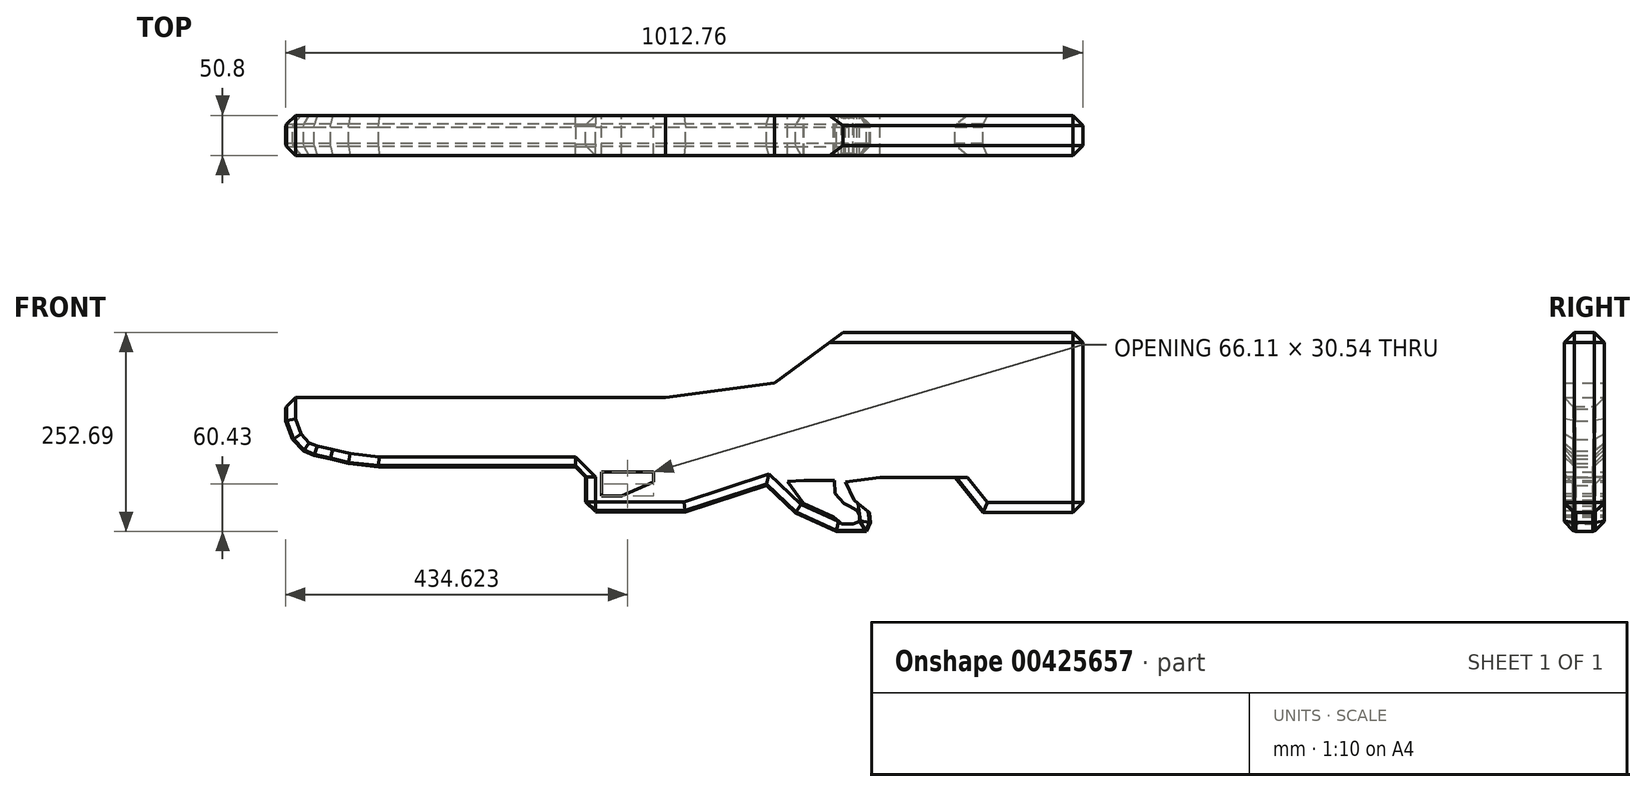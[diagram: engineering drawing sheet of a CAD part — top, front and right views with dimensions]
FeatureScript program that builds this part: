
annotation { "Feature Type Name" : "Feature", "Feature Type Description" : "" }
export const myFeature = defineFeature(function(context is Context, id is Id, definition is map)
    precondition{}
    {
        {
            var Q0;
            Q0=qCreatedBy(makeId("Front.planeOp"),FACE);
            var sketch = newSketch(context, id + "F0", { "sketchPlane" : qUnion([Q0])});
            skLineSegment(sketch, "E0", {"start": v(-56.13, -82.02) * mm, "end": v(-158.8, -115.37) * mm});
            skLineSegment(sketch, "E1", {"start": v(-158.8, -115.37) * mm, "end": v(-285.8, -115.37) * mm});
            skLineSegment(sketch, "E2", {"start": v(-285.8, -115.37) * mm, "end": v(-285.8, -58.22) * mm});
            skLineSegment(sketch, "E3", {"start": v(-285.8, -58.22) * mm, "end": v(-514.4, -58.22) * mm});
            skLineSegment(sketch, "E4", {"start": v(-666.8, 29.79) * mm, "end": v(-285.8, 29.79) * mm});
            skLineSegment(sketch, "E5", {"start": v(218.96, -116.33) * mm, "end": v(345.96, -116.33) * mm});
            skLineSegment(sketch, "E6", {"start": v(345.96, -116.33) * mm, "end": v(345.96, 112.27) * mm});
            skLineSegment(sketch, "E7", {"start": v(345.96, 112.27) * mm, "end": v(41.16, 112.27) * mm});
            skLineSegment(sketch, "E8", {"start": v(41.16, 112.27) * mm, "end": v(-45.72, 48.19) * mm});
            skLineSegment(sketch, "E9", {"start": v(-45.72, 48.19) * mm, "end": v(-184.2, 29.79) * mm});
            skLineSegment(sketch, "E10", {"start": v(-184.2, 29.79) * mm, "end": v(-285.8, 29.79) * mm});
            skLineSegment(sketch, "E11", {"start": v(-265.23, -64.72) * mm, "end": v(-265.23, -95.26) * mm});
            skLineSegment(sketch, "E12", {"start": v(-265.23, -95.26) * mm, "end": v(-239.83, -95.26) * mm});
            skLineSegment(sketch, "E13", {"start": v(-239.83, -95.26) * mm, "end": v(-199.12, -77.42) * mm});
            skLineSegment(sketch, "E14", {"start": v(-199.12, -77.42) * mm, "end": v(-199.12, -64.72) * mm});
            skLineSegment(sketch, "E15", {"start": v(-199.12, -64.72) * mm, "end": v(-265.23, -64.72) * mm});
            skLineSegment(sketch, "E16", {"start": v(-56.13, -82.02) * mm, "end": v(-19.03, -116.73) * mm});
            skLineSegment(sketch, "E17", {"start": v(-19.03, -116.73) * mm, "end": v(32.98, -140.42) * mm});
            skLineSegment(sketch, "E18", {"start": v(32.98, -140.42) * mm, "end": v(71.08, -140.42) * mm});
            skLineSegment(sketch, "E19", {"start": v(218.96, -116.33) * mm, "end": v(183.53, -71.5) * mm});
            skLineSegment(sketch, "E20", {"start": v(183.53, -71.5) * mm, "end": v(88.28, -71.5) * mm});
            skLineSegment(sketch, "E21", {"start": v(88.28, -71.5) * mm, "end": v(44.21, -77.35) * mm});
            skLineSegment(sketch, "E22", {"start": v(44.21, -77.35) * mm, "end": v(55.1, -100.3) * mm});
            skLineSegment(sketch, "E23", {"start": v(55.1, -100.3) * mm, "end": v(74.8, -116.33) * mm});
            skLineSegment(sketch, "E24", {"start": v(74.8, -116.33) * mm, "end": v(76.46, -128.92) * mm});
            skLineSegment(sketch, "E25", {"start": v(76.46, -128.92) * mm, "end": v(71.08, -140.42) * mm});
            skLineSegment(sketch, "E26", {"start": v(-29.05, -77.07) * mm, "end": v(-8.71, -104.67) * mm});
            skLineSegment(sketch, "E27", {"start": v(-8.71, -104.67) * mm, "end": v(29.47, -122.07) * mm});
            skLineSegment(sketch, "E28", {"start": v(42.4, -104.75) * mm, "end": v(31, -91.88) * mm});
            skLineSegment(sketch, "E29", {"start": v(31, -91.88) * mm, "end": v(30.46, -75.77) * mm});
            skLineSegment(sketch, "E30", {"start": v(30.46, -75.77) * mm, "end": v(-8.19, -75.77) * mm});
            skLineSegment(sketch, "E31", {"start": v(-8.19, -75.77) * mm, "end": v(-29.05, -77.07) * mm});
            skLineSegment(sketch, "E32", {"start": v(29.47, -122.07) * mm, "end": v(39.46, -130.68) * mm});
            skLineSegment(sketch, "E33", {"start": v(39.46, -130.68) * mm, "end": v(54.19, -130.68) * mm});
            skLineSegment(sketch, "E34", {"start": v(54.19, -130.68) * mm, "end": v(62.35, -127.97) * mm});
            skLineSegment(sketch, "E35", {"start": v(62.35, -127.97) * mm, "end": v(62.35, -122.07) * mm});
            skLineSegment(sketch, "E36", {"start": v(62.35, -122.07) * mm, "end": v(62.35, -119.65) * mm});
            skLineSegment(sketch, "E37", {"start": v(62.35, -119.65) * mm, "end": v(59.02, -113.61) * mm});
            skLineSegment(sketch, "E38", {"start": v(59.02, -113.61) * mm, "end": v(49.26, -108.1) * mm});
            skLineSegment(sketch, "E39", {"start": v(49.26, -108.1) * mm, "end": v(42.4, -104.75) * mm});
            skLineSegment(sketch, "E40", {"start": v(-666.8, 29.79) * mm, "end": v(-666.8, 0) * mm});
            skLineSegment(sketch, "E41", {"start": v(-666.8, 0) * mm, "end": v(-658, -23.58) * mm});
            skLineSegment(sketch, "E42", {"start": v(-658, -23.58) * mm, "end": v(-643.96, -38.44) * mm});
            skLineSegment(sketch, "E43", {"start": v(-514.4, -58.22) * mm, "end": v(-548.47, -58.22) * mm});
            skLineSegment(sketch, "E44", {"start": v(-548.47, -58.22) * mm, "end": v(-586.77, -53.93) * mm});
            skLineSegment(sketch, "E45", {"start": v(-586.77, -53.93) * mm, "end": v(-609.74, -48.34) * mm});
            skLineSegment(sketch, "E46", {"start": v(-609.74, -48.34) * mm, "end": v(-630.48, -44.18) * mm});
            skLineSegment(sketch, "E47", {"start": v(-630.48, -44.18) * mm, "end": v(-643.96, -38.44) * mm});
            skSolve(sketch);
        }
        {
            var Q0;
            Q0 = qSketchRegion(id + "F0", true);
            extrude(context, id + "F1", {"entities" : qUnion([Q0]), "depth" : 50.8 * mm});
        }
        {
            var Q0;
            Q0=makeQuery(id+"F1.opExtrude","CAP_EDGE",EDGE,{"disambiguationData":[OSD([sQuery(id+"F0.wireOp",EDGE,"E7")])],"isStart":true});
            var Q1;
            Q1=makeQuery(id+"F1.opExtrude","CAP_EDGE",EDGE,{"disambiguationData":[OSD([sQuery(id+"F0.wireOp",EDGE,"E7")])],"isStart":false});
            var Q2;
            Q2=makeQuery(id+"F1.opExtrude","CAP_EDGE",EDGE,{"disambiguationData":[OSD([sQuery(id+"F0.wireOp",EDGE,"E6")])],"isStart":false});
            var Q3;
            Q3=makeQuery(id+"F1.opExtrude","CAP_EDGE",EDGE,{"disambiguationData":[OSD([sQuery(id+"F0.wireOp",EDGE,"E6")])],"isStart":true});
            var Q4;
            Q4=makeQuery(id+"F1.opExtrude","SWEPT_EDGE",EDGE,{"disambiguationData":[OSD([sQuery(id+"F0.wireOp",EDGE,"E6"),sQuery(id+"F0.wireOp",EDGE,"E7")])]});
            var Q5;
            Q5=makeQuery(id+"F1.opExtrude","SWEPT_EDGE",EDGE,{"disambiguationData":[OSD([sQuery(id+"F0.wireOp",EDGE,"E5"),sQuery(id+"F0.wireOp",EDGE,"E6")])]});
            var Q6;
            Q6=makeQuery(id+"F1.opExtrude","CAP_EDGE",EDGE,{"disambiguationData":[OSD([sQuery(id+"F0.wireOp",EDGE,"E5")])],"isStart":true});
            var Q7;
            Q7=makeQuery(id+"F1.opExtrude","CAP_EDGE",EDGE,{"disambiguationData":[OSD([sQuery(id+"F0.wireOp",EDGE,"E5")])],"isStart":false});
            var Q8;
            Q8=makeQuery(id+"F1.opExtrude","CAP_EDGE",EDGE,{"disambiguationData":[OSD([sQuery(id+"F0.wireOp",EDGE,"0iQW84Cc-BR3S-5Jue-mCoC-AWeY4tAWd9hm")])],"isStart":true});
            var Q9;
            Q9=makeQuery(id+"F1.opExtrude","CAP_EDGE",EDGE,{"disambiguationData":[OSD([sQuery(id+"F0.wireOp",EDGE,"0iQW84Cc-BR3S-5Jue-mCoC-AWeY4tAWd9hm")])],"isStart":false});
            var Q10;
            Q10=makeQuery(id+"F1.opExtrude","CAP_EDGE",EDGE,{"disambiguationData":[OSD([sQuery(id+"F0.wireOp",EDGE,"J2oNxDXB-GuEv-2erL-x4Tu-Tdrz2HGzG4U1")])],"isStart":true});
            var Q11;
            Q11=makeQuery(id+"F1.opExtrude","CAP_EDGE",EDGE,{"disambiguationData":[OSD([sQuery(id+"F0.wireOp",EDGE,"J2oNxDXB-GuEv-2erL-x4Tu-Tdrz2HGzG4U1")])],"isStart":false});
            var Q12;
            Q12=makeQuery(id+"F1.opExtrude","CAP_EDGE",EDGE,{"disambiguationData":[OSD([sQuery(id+"F0.wireOp",EDGE,"E0")])],"isStart":true});
            var Q13;
            Q13=makeQuery(id+"F1.opExtrude","CAP_EDGE",EDGE,{"disambiguationData":[OSD([sQuery(id+"F0.wireOp",EDGE,"E0")])],"isStart":false});
            var Q14;
            Q14=makeQuery(id+"F1.opExtrude","CAP_EDGE",EDGE,{"disambiguationData":[OSD([sQuery(id+"F0.wireOp",EDGE,"E1")])],"isStart":true});
            var Q15;
            Q15=makeQuery(id+"F1.opExtrude","SWEPT_EDGE",EDGE,{"disambiguationData":[OSD([sQuery(id+"F0.wireOp",EDGE,"E1"),sQuery(id+"F0.wireOp",EDGE,"E2")])]});
            var Q16;
            Q16=makeQuery(id+"F1.opExtrude","CAP_EDGE",EDGE,{"disambiguationData":[OSD([sQuery(id+"F0.wireOp",EDGE,"E1")])],"isStart":false});
            var Q17;
            Q17=makeQuery(id+"F1.opExtrude","CAP_EDGE",EDGE,{"disambiguationData":[OSD([sQuery(id+"F0.wireOp",EDGE,"E3")])],"isStart":false});
            var Q18;
            Q18=makeQuery(id+"F1.opExtrude","CAP_EDGE",EDGE,{"disambiguationData":[OSD([sQuery(id+"F0.wireOp",EDGE,"E3")])],"isStart":true});
            var Q19;
            Q19=makeQuery(id+"F1.opExtrude","CAP_EDGE",EDGE,{"disambiguationData":[OSD([sQuery(id+"F0.wireOp",EDGE,"U8XlatA5-svrj-UKUK-BNE7-sDehN0CjtlMt")])],"isStart":false});
            var Q20;
            Q20=makeQuery(id+"F1.opExtrude","CAP_EDGE",EDGE,{"disambiguationData":[OSD([sQuery(id+"F0.wireOp",EDGE,"U8XlatA5-svrj-UKUK-BNE7-sDehN0CjtlMt")])],"isStart":true});
            var Q21;
            Q21=makeQuery(id+"F1.opExtrude","CAP_EDGE",EDGE,{"disambiguationData":[OSD([sQuery(id+"F0.wireOp",EDGE,"E2")])],"isStart":false});
            var Q22;
            Q22=makeQuery(id+"F1.opExtrude","CAP_EDGE",EDGE,{"disambiguationData":[OSD([sQuery(id+"F0.wireOp",EDGE,"E2")])],"isStart":true});
            var Q23;
            Q23=makeQuery(id+"F1.opExtrude","CAP_EDGE",EDGE,{"disambiguationData":[OSD([sQuery(id+"F0.wireOp",EDGE,"E19")])],"isStart":true});
            var Q24;
            Q24=makeQuery(id+"F1.opExtrude","CAP_EDGE",EDGE,{"disambiguationData":[OSD([sQuery(id+"F0.wireOp",EDGE,"E19")])],"isStart":false});
            var Q25;
            Q25=makeQuery(id+"F1.opExtrude","CAP_EDGE",EDGE,{"disambiguationData":[OSD([sQuery(id+"F0.wireOp",EDGE,"E16")])],"isStart":true});
            var Q26;
            Q26=makeQuery(id+"F1.opExtrude","CAP_EDGE",EDGE,{"disambiguationData":[OSD([sQuery(id+"F0.wireOp",EDGE,"E16")])],"isStart":false});
            var Q27;
            Q27=makeQuery(id+"F1.opExtrude","CAP_EDGE",EDGE,{"disambiguationData":[OSD([sQuery(id+"F0.wireOp",EDGE,"E17")])],"isStart":false});
            var Q28;
            Q28=makeQuery(id+"F1.opExtrude","CAP_EDGE",EDGE,{"disambiguationData":[OSD([sQuery(id+"F0.wireOp",EDGE,"E17")])],"isStart":true});
            var Q29;
            Q29=makeQuery(id+"F1.opExtrude","CAP_EDGE",EDGE,{"disambiguationData":[OSD([sQuery(id+"F0.wireOp",EDGE,"E18")])],"isStart":true});
            var Q30;
            Q30=makeQuery(id+"F1.opExtrude","CAP_EDGE",EDGE,{"disambiguationData":[OSD([sQuery(id+"F0.wireOp",EDGE,"E18")])],"isStart":false});
            var Q31;
            Q31=makeQuery(id+"F1.opExtrude","CAP_EDGE",EDGE,{"disambiguationData":[OSD([sQuery(id+"F0.wireOp",EDGE,"E25")])],"isStart":true});
            var Q32;
            Q32=makeQuery(id+"F1.opExtrude","CAP_EDGE",EDGE,{"disambiguationData":[OSD([sQuery(id+"F0.wireOp",EDGE,"E24")])],"isStart":true});
            var Q33;
            Q33=makeQuery(id+"F1.opExtrude","CAP_EDGE",EDGE,{"disambiguationData":[OSD([sQuery(id+"F0.wireOp",EDGE,"E25")])],"isStart":false});
            var Q34;
            Q34=makeQuery(id+"F1.opExtrude","CAP_EDGE",EDGE,{"disambiguationData":[OSD([sQuery(id+"F0.wireOp",EDGE,"E24")])],"isStart":false});
            var Q35;
            Q35=makeQuery(id+"F1.opExtrude","SWEPT_EDGE",EDGE,{"disambiguationData":[OSD([sQuery(id+"F0.wireOp",EDGE,"U8XlatA5-svrj-UKUK-BNE7-sDehN0CjtlMt"),sQuery(id+"F0.wireOp",EDGE,"E4")])]});
            var Q36;
            Q36=makeQuery(id+"F1.opExtrude","SWEPT_EDGE",EDGE,{"disambiguationData":[OSD([sQuery(id+"F0.wireOp",EDGE,"E3"),sQuery(id+"F0.wireOp",EDGE,"U8XlatA5-svrj-UKUK-BNE7-sDehN0CjtlMt")])]});
            var Q37;
            Q37=makeQuery(id+"F1.opExtrude","CAP_EDGE",EDGE,{"disambiguationData":[OSD([sQuery(id+"F0.wireOp",EDGE,"E44")])],"isStart":false});
            var Q38;
            Q38=makeQuery(id+"F1.opExtrude","CAP_EDGE",EDGE,{"disambiguationData":[OSD([sQuery(id+"F0.wireOp",EDGE,"E45")])],"isStart":false});
            var Q39;
            Q39=makeQuery(id+"F1.opExtrude","CAP_EDGE",EDGE,{"disambiguationData":[OSD([sQuery(id+"F0.wireOp",EDGE,"E47")])],"isStart":false});
            var Q40;
            Q40=makeQuery(id+"F1.opExtrude","CAP_EDGE",EDGE,{"disambiguationData":[OSD([sQuery(id+"F0.wireOp",EDGE,"E46")])],"isStart":false});
            var Q41;
            Q41=makeQuery(id+"F1.opExtrude","CAP_EDGE",EDGE,{"disambiguationData":[OSD([sQuery(id+"F0.wireOp",EDGE,"E42")])],"isStart":false});
            var Q42;
            Q42=makeQuery(id+"F1.opExtrude","CAP_EDGE",EDGE,{"disambiguationData":[OSD([sQuery(id+"F0.wireOp",EDGE,"E41")])],"isStart":false});
            var Q43;
            Q43=makeQuery(id+"F1.opExtrude","CAP_EDGE",EDGE,{"disambiguationData":[OSD([sQuery(id+"F0.wireOp",EDGE,"E40")])],"isStart":false});
            var Q44;
            Q44=makeQuery(id+"F1.opExtrude","CAP_EDGE",EDGE,{"disambiguationData":[OSD([sQuery(id+"F0.wireOp",EDGE,"E44")])],"isStart":true});
            var Q45;
            Q45=makeQuery(id+"F1.opExtrude","CAP_EDGE",EDGE,{"disambiguationData":[OSD([sQuery(id+"F0.wireOp",EDGE,"E45")])],"isStart":true});
            var Q46;
            Q46=makeQuery(id+"F1.opExtrude","CAP_EDGE",EDGE,{"disambiguationData":[OSD([sQuery(id+"F0.wireOp",EDGE,"E46")])],"isStart":true});
            var Q47;
            Q47=makeQuery(id+"F1.opExtrude","CAP_EDGE",EDGE,{"disambiguationData":[OSD([sQuery(id+"F0.wireOp",EDGE,"E47")])],"isStart":true});
            var Q48;
            Q48=makeQuery(id+"F1.opExtrude","CAP_EDGE",EDGE,{"disambiguationData":[OSD([sQuery(id+"F0.wireOp",EDGE,"E42")])],"isStart":true});
            var Q49;
            Q49=makeQuery(id+"F1.opExtrude","CAP_EDGE",EDGE,{"disambiguationData":[OSD([sQuery(id+"F0.wireOp",EDGE,"E41")])],"isStart":true});
            var Q50;
            Q50=makeQuery(id+"F1.opExtrude","CAP_EDGE",EDGE,{"disambiguationData":[OSD([sQuery(id+"F0.wireOp",EDGE,"E40")])],"isStart":true});
            chamfer(context, id + "F2", {"entities" : qUnion([Q0, Q1, Q2, Q3, Q4, Q5, Q6, Q7, Q8, Q9, Q10, Q11, Q12, Q13, Q14, Q15, Q16, Q17, Q18, Q19, Q20, Q21, Q22, Q23, Q24, Q25, Q26, Q27, Q28, Q29, Q30, Q31, Q32, Q33, Q34, Q35, Q36, Q37, Q38, Q39, Q40, Q41, Q42, Q43, Q44, Q45, Q46, Q47, Q48, Q49, Q50]), "width" : 12.7 * mm, "tangentPropagation" : true});
        }
        {
            var Q0;
            {var subQ0=sQuery(id+"F0.wireOp",EDGE,"E41");Q0=makeQuery(id+"F2.opChamfer","BLEND_EDGE",EDGE,{"blendedFrom":[makeQuery(id+"F1.opExtrude","CAP_EDGE",EDGE,{"disambiguationData":[OSD([subQ0])],"isStart":true}),makeQuery(id+"F1.opExtrude","SWEPT_FACE",FACE,{"disambiguationData":[OSD([subQ0])]})],"blendedInto":[makeQuery(id+"F1.opExtrude","SWEPT_FACE",FACE,{"disambiguationData":[OSD([subQ0])]})]});}
            var Q1;
            {var subQ0=sQuery(id+"F0.wireOp",EDGE,"E40");Q1=makeQuery(id+"F2.opChamfer","BLEND_EDGE",EDGE,{"blendedFrom":[makeQuery(id+"F1.opExtrude","CAP_EDGE",EDGE,{"disambiguationData":[OSD([subQ0])],"isStart":true}),makeQuery(id+"F1.opExtrude","SWEPT_FACE",FACE,{"disambiguationData":[OSD([subQ0])]})],"blendedInto":[makeQuery(id+"F1.opExtrude","SWEPT_FACE",FACE,{"disambiguationData":[OSD([subQ0])]})]});}
            var Q2;
            {var subQ0=sQuery(id+"F0.wireOp",EDGE,"E40");Q2=makeQuery(id+"F2.opChamfer","BLEND_EDGE",EDGE,{"blendedFrom":[makeQuery(id+"F1.opExtrude","CAP_EDGE",EDGE,{"disambiguationData":[OSD([subQ0])],"isStart":false}),makeQuery(id+"F1.opExtrude","SWEPT_FACE",FACE,{"disambiguationData":[OSD([subQ0])]})],"blendedInto":[makeQuery(id+"F1.opExtrude","SWEPT_FACE",FACE,{"disambiguationData":[OSD([subQ0])]})]});}
            var Q3;
            {var subQ0=sQuery(id+"F0.wireOp",EDGE,"E40");Q3=makeQuery(id+"F2.opChamfer","BLEND_EDGE",EDGE,{"blendedFrom":[makeQuery(id+"F1.opExtrude","SWEPT_EDGE",EDGE,{"disambiguationData":[OSD([sQuery(id+"F0.wireOp",EDGE,"E4"),subQ0])]}),makeQuery(id+"F1.opExtrude","SWEPT_FACE",FACE,{"disambiguationData":[OSD([subQ0])]})],"blendedInto":[makeQuery(id+"F1.opExtrude","SWEPT_FACE",FACE,{"disambiguationData":[OSD([subQ0])]})]});}
            var Q4;
            {var subQ0=sQuery(id+"F0.wireOp",EDGE,"E41");Q4=makeQuery(id+"F2.opChamfer","BLEND_EDGE",EDGE,{"blendedFrom":[makeQuery(id+"F1.opExtrude","CAP_EDGE",EDGE,{"disambiguationData":[OSD([subQ0])],"isStart":false}),makeQuery(id+"F1.opExtrude","SWEPT_FACE",FACE,{"disambiguationData":[OSD([subQ0])]})],"blendedInto":[makeQuery(id+"F1.opExtrude","SWEPT_FACE",FACE,{"disambiguationData":[OSD([subQ0])]})]});}
            var Q5;
            {var subQ0=sQuery(id+"F0.wireOp",EDGE,"E42");Q5=makeQuery(id+"F2.opChamfer","BLEND_EDGE",EDGE,{"blendedFrom":[makeQuery(id+"F1.opExtrude","CAP_EDGE",EDGE,{"disambiguationData":[OSD([subQ0])],"isStart":false}),makeQuery(id+"F1.opExtrude","SWEPT_FACE",FACE,{"disambiguationData":[OSD([subQ0])]})],"blendedInto":[makeQuery(id+"F1.opExtrude","SWEPT_FACE",FACE,{"disambiguationData":[OSD([subQ0])]})]});}
            var Q6;
            {var subQ0=sQuery(id+"F0.wireOp",EDGE,"E42");Q6=makeQuery(id+"F2.opChamfer","BLEND_EDGE",EDGE,{"blendedFrom":[makeQuery(id+"F1.opExtrude","CAP_EDGE",EDGE,{"disambiguationData":[OSD([subQ0])],"isStart":true}),makeQuery(id+"F1.opExtrude","SWEPT_FACE",FACE,{"disambiguationData":[OSD([subQ0])]})],"blendedInto":[makeQuery(id+"F1.opExtrude","SWEPT_FACE",FACE,{"disambiguationData":[OSD([subQ0])]})]});}
            var Q7;
            {var subQ0=sQuery(id+"F0.wireOp",EDGE,"E47");Q7=makeQuery(id+"F2.opChamfer","BLEND_EDGE",EDGE,{"blendedFrom":[makeQuery(id+"F1.opExtrude","CAP_EDGE",EDGE,{"disambiguationData":[OSD([subQ0])],"isStart":true}),makeQuery(id+"F1.opExtrude","SWEPT_FACE",FACE,{"disambiguationData":[OSD([subQ0])]})],"blendedInto":[makeQuery(id+"F1.opExtrude","SWEPT_FACE",FACE,{"disambiguationData":[OSD([subQ0])]})]});}
            var Q8;
            {var subQ0=sQuery(id+"F0.wireOp",EDGE,"E47");Q8=makeQuery(id+"F2.opChamfer","BLEND_EDGE",EDGE,{"blendedFrom":[makeQuery(id+"F1.opExtrude","CAP_EDGE",EDGE,{"disambiguationData":[OSD([subQ0])],"isStart":false}),makeQuery(id+"F1.opExtrude","SWEPT_FACE",FACE,{"disambiguationData":[OSD([subQ0])]})],"blendedInto":[makeQuery(id+"F1.opExtrude","SWEPT_FACE",FACE,{"disambiguationData":[OSD([subQ0])]})]});}
            var Q9;
            {var subQ0=sQuery(id+"F0.wireOp",EDGE,"E46");Q9=makeQuery(id+"F2.opChamfer","BLEND_EDGE",EDGE,{"blendedFrom":[makeQuery(id+"F1.opExtrude","CAP_EDGE",EDGE,{"disambiguationData":[OSD([subQ0])],"isStart":true}),makeQuery(id+"F1.opExtrude","SWEPT_FACE",FACE,{"disambiguationData":[OSD([subQ0])]})],"blendedInto":[makeQuery(id+"F1.opExtrude","SWEPT_FACE",FACE,{"disambiguationData":[OSD([subQ0])]})]});}
            var Q10;
            {var subQ0=sQuery(id+"F0.wireOp",EDGE,"E45");Q10=makeQuery(id+"F2.opChamfer","BLEND_EDGE",EDGE,{"blendedFrom":[makeQuery(id+"F1.opExtrude","CAP_EDGE",EDGE,{"disambiguationData":[OSD([subQ0])],"isStart":true}),makeQuery(id+"F1.opExtrude","SWEPT_FACE",FACE,{"disambiguationData":[OSD([subQ0])]})],"blendedInto":[makeQuery(id+"F1.opExtrude","SWEPT_FACE",FACE,{"disambiguationData":[OSD([subQ0])]})]});}
            var Q11;
            {var subQ0=sQuery(id+"F0.wireOp",EDGE,"E44");Q11=makeQuery(id+"F2.opChamfer","BLEND_EDGE",EDGE,{"blendedFrom":[makeQuery(id+"F1.opExtrude","CAP_EDGE",EDGE,{"disambiguationData":[OSD([subQ0])],"isStart":true}),makeQuery(id+"F1.opExtrude","SWEPT_FACE",FACE,{"disambiguationData":[OSD([subQ0])]})],"blendedInto":[makeQuery(id+"F1.opExtrude","SWEPT_FACE",FACE,{"disambiguationData":[OSD([subQ0])]})]});}
            var Q12;
            {var subQ0=sQuery(id+"F0.wireOp",EDGE,"E46");Q12=makeQuery(id+"F2.opChamfer","BLEND_EDGE",EDGE,{"blendedFrom":[makeQuery(id+"F1.opExtrude","CAP_EDGE",EDGE,{"disambiguationData":[OSD([subQ0])],"isStart":false}),makeQuery(id+"F1.opExtrude","SWEPT_FACE",FACE,{"disambiguationData":[OSD([subQ0])]})],"blendedInto":[makeQuery(id+"F1.opExtrude","SWEPT_FACE",FACE,{"disambiguationData":[OSD([subQ0])]})]});}
            var Q13;
            {var subQ0=sQuery(id+"F0.wireOp",EDGE,"E45");Q13=makeQuery(id+"F2.opChamfer","BLEND_EDGE",EDGE,{"blendedFrom":[makeQuery(id+"F1.opExtrude","CAP_EDGE",EDGE,{"disambiguationData":[OSD([subQ0])],"isStart":false}),makeQuery(id+"F1.opExtrude","SWEPT_FACE",FACE,{"disambiguationData":[OSD([subQ0])]})],"blendedInto":[makeQuery(id+"F1.opExtrude","SWEPT_FACE",FACE,{"disambiguationData":[OSD([subQ0])]})]});}
            var Q14;
            {var subQ0=sQuery(id+"F0.wireOp",EDGE,"E44");Q14=makeQuery(id+"F2.opChamfer","BLEND_EDGE",EDGE,{"blendedFrom":[makeQuery(id+"F1.opExtrude","CAP_EDGE",EDGE,{"disambiguationData":[OSD([subQ0])],"isStart":false}),makeQuery(id+"F1.opExtrude","SWEPT_FACE",FACE,{"disambiguationData":[OSD([subQ0])]})],"blendedInto":[makeQuery(id+"F1.opExtrude","SWEPT_FACE",FACE,{"disambiguationData":[OSD([subQ0])]})]});}
            var Q15;
            {var subQ0=sQuery(id+"F0.wireOp",EDGE,"E43");var subQ1=sQuery(id+"F0.wireOp",EDGE,"E3");Q15=makeQuery(id+"F2.opChamfer","BLEND_EDGE",EDGE,{"blendedFrom":[makeQuery(id+"F1.opExtrude","CAP_EDGE",EDGE,{"disambiguationData":[OSD([subQ1,subQ0])],"isStart":false}),makeQuery(id+"F1.opExtrude","SWEPT_FACE",FACE,{"disambiguationData":[OSD([subQ1,subQ0])]})],"blendedInto":[makeQuery(id+"F1.opExtrude","SWEPT_FACE",FACE,{"disambiguationData":[OSD([subQ1,subQ0])]})]});}
            var Q16;
            {var subQ0=sQuery(id+"F0.wireOp",EDGE,"E43");var subQ1=sQuery(id+"F0.wireOp",EDGE,"E3");Q16=makeQuery(id+"F2.opChamfer","BLEND_EDGE",EDGE,{"blendedFrom":[makeQuery(id+"F1.opExtrude","CAP_EDGE",EDGE,{"disambiguationData":[OSD([subQ1,subQ0])],"isStart":true}),makeQuery(id+"F1.opExtrude","SWEPT_FACE",FACE,{"disambiguationData":[OSD([subQ1,subQ0])]})],"blendedInto":[makeQuery(id+"F1.opExtrude","SWEPT_FACE",FACE,{"disambiguationData":[OSD([subQ1,subQ0])]})]});}
            var Q17;
            {var subQ0=sQuery(id+"F0.wireOp",EDGE,"E3");var subQ1=sQuery(id+"F0.wireOp",EDGE,"E2");Q17=makeQuery(id+"F2.opChamfer","BLEND_EDGE",EDGE,{"blendedFrom":[makeQuery(id+"F1.opExtrude","CAP_VERTEX",VERTEX,{"disambiguationData":[OSD([subQ1,subQ0])],"isStart":true}),makeQuery(id+"F1.opExtrude","SWEPT_EDGE",EDGE,{"disambiguationData":[OSD([subQ1,subQ0])]})],"blendedInto":[]});}
            var Q18;
            {var subQ0=sQuery(id+"F0.wireOp",EDGE,"E3");var subQ1=sQuery(id+"F0.wireOp",EDGE,"E2");Q18=makeQuery(id+"F2.opChamfer","BLEND_EDGE",EDGE,{"blendedFrom":[makeQuery(id+"F1.opExtrude","CAP_VERTEX",VERTEX,{"disambiguationData":[OSD([subQ1,subQ0])],"isStart":false}),makeQuery(id+"F1.opExtrude","SWEPT_EDGE",EDGE,{"disambiguationData":[OSD([subQ1,subQ0])]})],"blendedInto":[]});}
            var Q19;
            {var subQ0=sQuery(id+"F0.wireOp",EDGE,"E2");Q19=makeQuery(id+"F2.opChamfer","BLEND_EDGE",EDGE,{"blendedFrom":[makeQuery(id+"F1.opExtrude","CAP_EDGE",EDGE,{"disambiguationData":[OSD([subQ0])],"isStart":true}),makeQuery(id+"F1.opExtrude","SWEPT_FACE",FACE,{"disambiguationData":[OSD([subQ0])]})],"blendedInto":[makeQuery(id+"F1.opExtrude","SWEPT_FACE",FACE,{"disambiguationData":[OSD([subQ0])]})]});}
            var Q20;
            {var subQ0=sQuery(id+"F0.wireOp",EDGE,"E2");Q20=makeQuery(id+"F2.opChamfer","BLEND_EDGE",EDGE,{"blendedFrom":[makeQuery(id+"F1.opExtrude","CAP_EDGE",EDGE,{"disambiguationData":[OSD([subQ0])],"isStart":false}),makeQuery(id+"F1.opExtrude","SWEPT_FACE",FACE,{"disambiguationData":[OSD([subQ0])]})],"blendedInto":[makeQuery(id+"F1.opExtrude","SWEPT_FACE",FACE,{"disambiguationData":[OSD([subQ0])]})]});}
            var Q21;
            {var subQ0=sQuery(id+"F0.wireOp",EDGE,"E2");var subQ1=sQuery(id+"F0.wireOp",EDGE,"E1");Q21=makeQuery(id+"F2.opChamfer","BLEND_EDGE",EDGE,{"blendedFrom":[makeQuery(id+"F1.opExtrude","CAP_VERTEX",VERTEX,{"disambiguationData":[OSD([subQ1,subQ0])],"isStart":true}),makeQuery(id+"F1.opExtrude","SWEPT_EDGE",EDGE,{"disambiguationData":[OSD([subQ1,subQ0])]})],"blendedInto":[]});}
            var Q22;
            {var subQ0=sQuery(id+"F0.wireOp",EDGE,"E2");var subQ1=sQuery(id+"F0.wireOp",EDGE,"E1");Q22=makeQuery(id+"F2.opChamfer","BLEND_EDGE",EDGE,{"blendedFrom":[makeQuery(id+"F1.opExtrude","CAP_VERTEX",VERTEX,{"disambiguationData":[OSD([subQ1,subQ0])],"isStart":false}),makeQuery(id+"F1.opExtrude","SWEPT_EDGE",EDGE,{"disambiguationData":[OSD([subQ1,subQ0])]})],"blendedInto":[]});}
            var Q23;
            {var subQ0=sQuery(id+"F0.wireOp",EDGE,"E1");Q23=makeQuery(id+"F2.opChamfer","BLEND_EDGE",EDGE,{"blendedFrom":[makeQuery(id+"F1.opExtrude","CAP_EDGE",EDGE,{"disambiguationData":[OSD([subQ0])],"isStart":true}),makeQuery(id+"F1.opExtrude","SWEPT_FACE",FACE,{"disambiguationData":[OSD([subQ0])]})],"blendedInto":[makeQuery(id+"F1.opExtrude","SWEPT_FACE",FACE,{"disambiguationData":[OSD([subQ0])]})]});}
            var Q24;
            {var subQ0=sQuery(id+"F0.wireOp",EDGE,"E1");Q24=makeQuery(id+"F2.opChamfer","BLEND_EDGE",EDGE,{"blendedFrom":[makeQuery(id+"F1.opExtrude","CAP_EDGE",EDGE,{"disambiguationData":[OSD([subQ0])],"isStart":false}),makeQuery(id+"F1.opExtrude","SWEPT_FACE",FACE,{"disambiguationData":[OSD([subQ0])]})],"blendedInto":[makeQuery(id+"F1.opExtrude","SWEPT_FACE",FACE,{"disambiguationData":[OSD([subQ0])]})]});}
            var Q25;
            {var subQ0=sQuery(id+"F0.wireOp",EDGE,"E0");Q25=makeQuery(id+"F2.opChamfer","BLEND_EDGE",EDGE,{"blendedFrom":[makeQuery(id+"F1.opExtrude","CAP_EDGE",EDGE,{"disambiguationData":[OSD([subQ0])],"isStart":true}),makeQuery(id+"F1.opExtrude","SWEPT_FACE",FACE,{"disambiguationData":[OSD([subQ0])]})],"blendedInto":[makeQuery(id+"F1.opExtrude","SWEPT_FACE",FACE,{"disambiguationData":[OSD([subQ0])]})]});}
            var Q26;
            {var subQ0=sQuery(id+"F0.wireOp",EDGE,"E0");Q26=makeQuery(id+"F2.opChamfer","BLEND_EDGE",EDGE,{"blendedFrom":[makeQuery(id+"F1.opExtrude","CAP_EDGE",EDGE,{"disambiguationData":[OSD([subQ0])],"isStart":false}),makeQuery(id+"F1.opExtrude","SWEPT_FACE",FACE,{"disambiguationData":[OSD([subQ0])]})],"blendedInto":[makeQuery(id+"F1.opExtrude","SWEPT_FACE",FACE,{"disambiguationData":[OSD([subQ0])]})]});}
            var Q27;
            {var subQ0=sQuery(id+"F0.wireOp",EDGE,"E16");Q27=makeQuery(id+"F2.opChamfer","BLEND_EDGE",EDGE,{"blendedFrom":[makeQuery(id+"F1.opExtrude","CAP_EDGE",EDGE,{"disambiguationData":[OSD([subQ0])],"isStart":true}),makeQuery(id+"F1.opExtrude","SWEPT_FACE",FACE,{"disambiguationData":[OSD([subQ0])]})],"blendedInto":[makeQuery(id+"F1.opExtrude","SWEPT_FACE",FACE,{"disambiguationData":[OSD([subQ0])]})]});}
            var Q28;
            {var subQ0=sQuery(id+"F0.wireOp",EDGE,"E16");Q28=makeQuery(id+"F2.opChamfer","BLEND_EDGE",EDGE,{"blendedFrom":[makeQuery(id+"F1.opExtrude","CAP_EDGE",EDGE,{"disambiguationData":[OSD([subQ0])],"isStart":false}),makeQuery(id+"F1.opExtrude","SWEPT_FACE",FACE,{"disambiguationData":[OSD([subQ0])]})],"blendedInto":[makeQuery(id+"F1.opExtrude","SWEPT_FACE",FACE,{"disambiguationData":[OSD([subQ0])]})]});}
            var Q29;
            {var subQ0=sQuery(id+"F0.wireOp",EDGE,"E17");Q29=makeQuery(id+"F2.opChamfer","BLEND_EDGE",EDGE,{"blendedFrom":[makeQuery(id+"F1.opExtrude","CAP_EDGE",EDGE,{"disambiguationData":[OSD([subQ0])],"isStart":false}),makeQuery(id+"F1.opExtrude","SWEPT_FACE",FACE,{"disambiguationData":[OSD([subQ0])]})],"blendedInto":[makeQuery(id+"F1.opExtrude","SWEPT_FACE",FACE,{"disambiguationData":[OSD([subQ0])]})]});}
            var Q30;
            {var subQ0=sQuery(id+"F0.wireOp",EDGE,"E17");Q30=makeQuery(id+"F2.opChamfer","BLEND_EDGE",EDGE,{"blendedFrom":[makeQuery(id+"F1.opExtrude","CAP_EDGE",EDGE,{"disambiguationData":[OSD([subQ0])],"isStart":true}),makeQuery(id+"F1.opExtrude","SWEPT_FACE",FACE,{"disambiguationData":[OSD([subQ0])]})],"blendedInto":[makeQuery(id+"F1.opExtrude","SWEPT_FACE",FACE,{"disambiguationData":[OSD([subQ0])]})]});}
            var Q31;
            {var subQ0=sQuery(id+"F0.wireOp",EDGE,"E18");Q31=makeQuery(id+"F2.opChamfer","BLEND_EDGE",EDGE,{"blendedFrom":[makeQuery(id+"F1.opExtrude","CAP_EDGE",EDGE,{"disambiguationData":[OSD([subQ0])],"isStart":true}),makeQuery(id+"F1.opExtrude","SWEPT_FACE",FACE,{"disambiguationData":[OSD([subQ0])]})],"blendedInto":[makeQuery(id+"F1.opExtrude","SWEPT_FACE",FACE,{"disambiguationData":[OSD([subQ0])]})]});}
            var Q32;
            {var subQ0=sQuery(id+"F0.wireOp",EDGE,"E18");Q32=makeQuery(id+"F2.opChamfer","BLEND_EDGE",EDGE,{"blendedFrom":[makeQuery(id+"F1.opExtrude","CAP_EDGE",EDGE,{"disambiguationData":[OSD([subQ0])],"isStart":false}),makeQuery(id+"F1.opExtrude","SWEPT_FACE",FACE,{"disambiguationData":[OSD([subQ0])]})],"blendedInto":[makeQuery(id+"F1.opExtrude","SWEPT_FACE",FACE,{"disambiguationData":[OSD([subQ0])]})]});}
            var Q33;
            {var subQ0=sQuery(id+"F0.wireOp",EDGE,"E25");Q33=makeQuery(id+"F2.opChamfer","BLEND_EDGE",EDGE,{"blendedFrom":[makeQuery(id+"F1.opExtrude","CAP_EDGE",EDGE,{"disambiguationData":[OSD([subQ0])],"isStart":true}),makeQuery(id+"F1.opExtrude","SWEPT_FACE",FACE,{"disambiguationData":[OSD([subQ0])]})],"blendedInto":[makeQuery(id+"F1.opExtrude","SWEPT_FACE",FACE,{"disambiguationData":[OSD([subQ0])]})]});}
            var Q34;
            {var subQ0=sQuery(id+"F0.wireOp",EDGE,"E24");Q34=makeQuery(id+"F2.opChamfer","BLEND_EDGE",EDGE,{"blendedFrom":[makeQuery(id+"F1.opExtrude","CAP_EDGE",EDGE,{"disambiguationData":[OSD([subQ0])],"isStart":true}),makeQuery(id+"F1.opExtrude","SWEPT_FACE",FACE,{"disambiguationData":[OSD([subQ0])]})],"blendedInto":[makeQuery(id+"F1.opExtrude","SWEPT_FACE",FACE,{"disambiguationData":[OSD([subQ0])]})]});}
            var Q35;
            {var subQ0=sQuery(id+"F0.wireOp",EDGE,"E25");Q35=makeQuery(id+"F2.opChamfer","BLEND_EDGE",EDGE,{"blendedFrom":[makeQuery(id+"F1.opExtrude","CAP_EDGE",EDGE,{"disambiguationData":[OSD([subQ0])],"isStart":false}),makeQuery(id+"F1.opExtrude","SWEPT_FACE",FACE,{"disambiguationData":[OSD([subQ0])]})],"blendedInto":[makeQuery(id+"F1.opExtrude","SWEPT_FACE",FACE,{"disambiguationData":[OSD([subQ0])]})]});}
            var Q36;
            {var subQ0=sQuery(id+"F0.wireOp",EDGE,"E24");Q36=makeQuery(id+"F2.opChamfer","BLEND_EDGE",EDGE,{"blendedFrom":[makeQuery(id+"F1.opExtrude","CAP_EDGE",EDGE,{"disambiguationData":[OSD([subQ0])],"isStart":false}),makeQuery(id+"F1.opExtrude","SWEPT_FACE",FACE,{"disambiguationData":[OSD([subQ0])]})],"blendedInto":[makeQuery(id+"F1.opExtrude","SWEPT_FACE",FACE,{"disambiguationData":[OSD([subQ0])]})]});}
            chamfer(context, id + "F3", {"entities" : qUnion([Q0, Q1, Q2, Q3, Q4, Q5, Q6, Q7, Q8, Q9, Q10, Q11, Q12, Q13, Q14, Q15, Q16, Q17, Q18, Q19, Q20, Q21, Q22, Q23, Q24, Q25, Q26, Q27, Q28, Q29, Q30, Q31, Q32, Q33, Q34, Q35, Q36]), "width" : 5.08 * mm, "tangentPropagation" : true});
        }
        {
            var Q0;
            {var subQ0=sQuery(id+"F0.wireOp",EDGE,"E16");Q0=makeQuery(id+"F2.opChamfer","BLEND_EDGE",EDGE,{"blendedFrom":[makeQuery(id+"F1.opExtrude","CAP_EDGE",EDGE,{"disambiguationData":[OSD([subQ0])],"isStart":false}),makeQuery(id+"F1.opExtrude","SWEPT_FACE",FACE,{"disambiguationData":[OSD([subQ0])]})],"blendedInto":[makeQuery(id+"F1.opExtrude","SWEPT_FACE",FACE,{"disambiguationData":[OSD([subQ0])]})]});}
            var Q1;
            {var subQ0=sQuery(id+"F0.wireOp",EDGE,"E17");Q1=makeQuery(id+"F2.opChamfer","BLEND_EDGE",EDGE,{"blendedFrom":[makeQuery(id+"F1.opExtrude","CAP_EDGE",EDGE,{"disambiguationData":[OSD([subQ0])],"isStart":false}),makeQuery(id+"F1.opExtrude","SWEPT_FACE",FACE,{"disambiguationData":[OSD([subQ0])]})],"blendedInto":[makeQuery(id+"F1.opExtrude","SWEPT_FACE",FACE,{"disambiguationData":[OSD([subQ0])]})]});}
            var Q2;
            {var subQ0=sQuery(id+"F0.wireOp",EDGE,"E17");Q2=makeQuery(id+"F2.opChamfer","BLEND_EDGE",EDGE,{"blendedFrom":[makeQuery(id+"F1.opExtrude","CAP_EDGE",EDGE,{"disambiguationData":[OSD([subQ0])],"isStart":true}),makeQuery(id+"F1.opExtrude","SWEPT_FACE",FACE,{"disambiguationData":[OSD([subQ0])]})],"blendedInto":[makeQuery(id+"F1.opExtrude","SWEPT_FACE",FACE,{"disambiguationData":[OSD([subQ0])]})]});}
            var Q3;
            {var subQ0=sQuery(id+"F0.wireOp",EDGE,"E16");Q3=makeQuery(id+"F2.opChamfer","BLEND_EDGE",EDGE,{"blendedFrom":[makeQuery(id+"F1.opExtrude","CAP_EDGE",EDGE,{"disambiguationData":[OSD([subQ0])],"isStart":true}),makeQuery(id+"F1.opExtrude","SWEPT_FACE",FACE,{"disambiguationData":[OSD([subQ0])]})],"blendedInto":[makeQuery(id+"F1.opExtrude","SWEPT_FACE",FACE,{"disambiguationData":[OSD([subQ0])]})]});}
            var Q4;
            {var subQ0=sQuery(id+"F0.wireOp",EDGE,"E18");Q4=makeQuery(id+"F2.opChamfer","BLEND_EDGE",EDGE,{"blendedFrom":[makeQuery(id+"F1.opExtrude","CAP_EDGE",EDGE,{"disambiguationData":[OSD([subQ0])],"isStart":true}),makeQuery(id+"F1.opExtrude","SWEPT_FACE",FACE,{"disambiguationData":[OSD([subQ0])]})],"blendedInto":[makeQuery(id+"F1.opExtrude","SWEPT_FACE",FACE,{"disambiguationData":[OSD([subQ0])]})]});}
            var Q5;
            {var subQ0=sQuery(id+"F0.wireOp",EDGE,"E18");Q5=makeQuery(id+"F2.opChamfer","BLEND_EDGE",EDGE,{"blendedFrom":[makeQuery(id+"F1.opExtrude","CAP_EDGE",EDGE,{"disambiguationData":[OSD([subQ0])],"isStart":false}),makeQuery(id+"F1.opExtrude","SWEPT_FACE",FACE,{"disambiguationData":[OSD([subQ0])]})],"blendedInto":[makeQuery(id+"F1.opExtrude","SWEPT_FACE",FACE,{"disambiguationData":[OSD([subQ0])]})]});}
            var Q6;
            {var subQ0=sQuery(id+"F0.wireOp",EDGE,"E22");Q6=makeQuery(id+"F3.opChamfer","BLEND_EDGE",EDGE,{"blendedFrom":[makeQuery(id+"F1.opExtrude","CAP_EDGE",EDGE,{"disambiguationData":[OSD([subQ0])],"isStart":false}),makeQuery(id+"F1.opExtrude","SWEPT_FACE",FACE,{"disambiguationData":[OSD([subQ0])]})],"blendedInto":[makeQuery(id+"F1.opExtrude","SWEPT_FACE",FACE,{"disambiguationData":[OSD([subQ0])]})]});}
            var Q7;
            {var subQ0=sQuery(id+"F0.wireOp",EDGE,"E23");var subQ1=sQuery(id+"F0.wireOp",EDGE,"E22");Q7=makeQuery(id+"F3.opChamfer","BLEND_EDGE",EDGE,{"blendedFrom":[makeQuery(id+"F1.opExtrude","CAP_VERTEX",VERTEX,{"disambiguationData":[OSD([subQ1,subQ0])],"isStart":false}),makeQuery(id+"F1.opExtrude","SWEPT_EDGE",EDGE,{"disambiguationData":[OSD([subQ1,subQ0])]})],"blendedInto":[]});}
            var Q8;
            {var subQ0=sQuery(id+"F0.wireOp",EDGE,"E23");Q8=makeQuery(id+"F3.opChamfer","BLEND_EDGE",EDGE,{"blendedFrom":[makeQuery(id+"F1.opExtrude","CAP_EDGE",EDGE,{"disambiguationData":[OSD([subQ0])],"isStart":false}),makeQuery(id+"F1.opExtrude","SWEPT_FACE",FACE,{"disambiguationData":[OSD([subQ0])]})],"blendedInto":[makeQuery(id+"F1.opExtrude","SWEPT_FACE",FACE,{"disambiguationData":[OSD([subQ0])]})]});}
            var Q9;
            {var subQ0=sQuery(id+"F0.wireOp",EDGE,"E24");Q9=makeQuery(id+"F2.opChamfer","BLEND_EDGE",EDGE,{"blendedFrom":[makeQuery(id+"F1.opExtrude","CAP_EDGE",EDGE,{"disambiguationData":[OSD([subQ0])],"isStart":false}),makeQuery(id+"F1.opExtrude","SWEPT_FACE",FACE,{"disambiguationData":[OSD([subQ0])]})],"blendedInto":[makeQuery(id+"F1.opExtrude","SWEPT_FACE",FACE,{"disambiguationData":[OSD([subQ0])]})]});}
            var Q10;
            {var subQ0=sQuery(id+"F0.wireOp",EDGE,"E25");Q10=makeQuery(id+"F2.opChamfer","BLEND_EDGE",EDGE,{"blendedFrom":[makeQuery(id+"F1.opExtrude","CAP_EDGE",EDGE,{"disambiguationData":[OSD([subQ0])],"isStart":false}),makeQuery(id+"F1.opExtrude","SWEPT_FACE",FACE,{"disambiguationData":[OSD([subQ0])]})],"blendedInto":[makeQuery(id+"F1.opExtrude","SWEPT_FACE",FACE,{"disambiguationData":[OSD([subQ0])]})]});}
            var Q11;
            {var subQ0=sQuery(id+"F0.wireOp",EDGE,"E24");Q11=makeQuery(id+"F2.opChamfer","BLEND_EDGE",EDGE,{"blendedFrom":[makeQuery(id+"F1.opExtrude","CAP_EDGE",EDGE,{"disambiguationData":[OSD([subQ0])],"isStart":true}),makeQuery(id+"F1.opExtrude","SWEPT_FACE",FACE,{"disambiguationData":[OSD([subQ0])]})],"blendedInto":[makeQuery(id+"F1.opExtrude","SWEPT_FACE",FACE,{"disambiguationData":[OSD([subQ0])]})]});}
            var Q12;
            {var subQ0=sQuery(id+"F0.wireOp",EDGE,"E25");Q12=makeQuery(id+"F2.opChamfer","BLEND_EDGE",EDGE,{"blendedFrom":[makeQuery(id+"F1.opExtrude","CAP_EDGE",EDGE,{"disambiguationData":[OSD([subQ0])],"isStart":true}),makeQuery(id+"F1.opExtrude","SWEPT_FACE",FACE,{"disambiguationData":[OSD([subQ0])]})],"blendedInto":[makeQuery(id+"F1.opExtrude","SWEPT_FACE",FACE,{"disambiguationData":[OSD([subQ0])]})]});}
            var Q13;
            {var subQ0=sQuery(id+"F0.wireOp",EDGE,"E23");Q13=makeQuery(id+"F3.opChamfer","BLEND_EDGE",EDGE,{"blendedFrom":[makeQuery(id+"F1.opExtrude","CAP_EDGE",EDGE,{"disambiguationData":[OSD([subQ0])],"isStart":true}),makeQuery(id+"F1.opExtrude","SWEPT_FACE",FACE,{"disambiguationData":[OSD([subQ0])]})],"blendedInto":[makeQuery(id+"F1.opExtrude","SWEPT_FACE",FACE,{"disambiguationData":[OSD([subQ0])]})]});}
            var Q14;
            {var subQ0=sQuery(id+"F0.wireOp",EDGE,"E23");var subQ1=sQuery(id+"F0.wireOp",EDGE,"E22");Q14=makeQuery(id+"F3.opChamfer","BLEND_EDGE",EDGE,{"blendedFrom":[makeQuery(id+"F1.opExtrude","CAP_VERTEX",VERTEX,{"disambiguationData":[OSD([subQ1,subQ0])],"isStart":true}),makeQuery(id+"F1.opExtrude","SWEPT_EDGE",EDGE,{"disambiguationData":[OSD([subQ1,subQ0])]})],"blendedInto":[]});}
            var Q15;
            {var subQ0=sQuery(id+"F0.wireOp",EDGE,"E22");Q15=makeQuery(id+"F3.opChamfer","BLEND_EDGE",EDGE,{"blendedFrom":[makeQuery(id+"F1.opExtrude","CAP_EDGE",EDGE,{"disambiguationData":[OSD([subQ0])],"isStart":true}),makeQuery(id+"F1.opExtrude","CAP_FACE",FACE,{"disambiguationData":[OSD([sQuery(id+"F0.wireOp",EDGE,"E0"),sQuery(id+"F0.wireOp",EDGE,"E1"),sQuery(id+"F0.wireOp",EDGE,"E2"),sQuery(id+"F0.wireOp",EDGE,"E3"),sQuery(id+"F0.wireOp",EDGE,"U8XlatA5-svrj-UKUK-BNE7-sDehN0CjtlMt"),sQuery(id+"F0.wireOp",EDGE,"E4"),sQuery(id+"F0.wireOp",EDGE,"E5"),sQuery(id+"F0.wireOp",EDGE,"E6"),sQuery(id+"F0.wireOp",EDGE,"E7"),sQuery(id+"F0.wireOp",EDGE,"E8"),sQuery(id+"F0.wireOp",EDGE,"E9"),sQuery(id+"F0.wireOp",EDGE,"E10"),sQuery(id+"F0.wireOp",EDGE,"E11"),sQuery(id+"F0.wireOp",EDGE,"E12"),sQuery(id+"F0.wireOp",EDGE,"E13"),sQuery(id+"F0.wireOp",EDGE,"E14"),sQuery(id+"F0.wireOp",EDGE,"E15"),sQuery(id+"F0.wireOp",EDGE,"E16"),sQuery(id+"F0.wireOp",EDGE,"E17"),sQuery(id+"F0.wireOp",EDGE,"E18"),sQuery(id+"F0.wireOp",EDGE,"E19"),sQuery(id+"F0.wireOp",EDGE,"E20"),sQuery(id+"F0.wireOp",EDGE,"E21"),subQ0,sQuery(id+"F0.wireOp",EDGE,"E23"),sQuery(id+"F0.wireOp",EDGE,"E24"),sQuery(id+"F0.wireOp",EDGE,"E25"),sQuery(id+"F0.wireOp",EDGE,"E26"),sQuery(id+"F0.wireOp",EDGE,"E27"),sQuery(id+"F0.wireOp",EDGE,"uk7PX5xF-f4ir-d9Fz-fdzY-7k4JSw0t9sw8"),sQuery(id+"F0.wireOp",EDGE,"4LPARoRI-8ECf-zc7A-Vkg7-1xuqQKTpim5R"),sQuery(id+"F0.wireOp",EDGE,"JqhvHDZe-7HvT-5HnW-5w5B-O84xCgJDLy5n"),sQuery(id+"F0.wireOp",EDGE,"E28"),sQuery(id+"F0.wireOp",EDGE,"E29"),sQuery(id+"F0.wireOp",EDGE,"E30"),sQuery(id+"F0.wireOp",EDGE,"E31")])],"isStart":true})],"blendedInto":[makeQuery(id+"F1.opExtrude","CAP_FACE",FACE,{"disambiguationData":[OSD([sQuery(id+"F0.wireOp",EDGE,"E0"),sQuery(id+"F0.wireOp",EDGE,"E1"),sQuery(id+"F0.wireOp",EDGE,"E2"),sQuery(id+"F0.wireOp",EDGE,"E3"),sQuery(id+"F0.wireOp",EDGE,"U8XlatA5-svrj-UKUK-BNE7-sDehN0CjtlMt"),sQuery(id+"F0.wireOp",EDGE,"E4"),sQuery(id+"F0.wireOp",EDGE,"E5"),sQuery(id+"F0.wireOp",EDGE,"E6"),sQuery(id+"F0.wireOp",EDGE,"E7"),sQuery(id+"F0.wireOp",EDGE,"E8"),sQuery(id+"F0.wireOp",EDGE,"E9"),sQuery(id+"F0.wireOp",EDGE,"E10"),sQuery(id+"F0.wireOp",EDGE,"E11"),sQuery(id+"F0.wireOp",EDGE,"E12"),sQuery(id+"F0.wireOp",EDGE,"E13"),sQuery(id+"F0.wireOp",EDGE,"E14"),sQuery(id+"F0.wireOp",EDGE,"E15"),sQuery(id+"F0.wireOp",EDGE,"E16"),sQuery(id+"F0.wireOp",EDGE,"E17"),sQuery(id+"F0.wireOp",EDGE,"E18"),sQuery(id+"F0.wireOp",EDGE,"E19"),sQuery(id+"F0.wireOp",EDGE,"E20"),sQuery(id+"F0.wireOp",EDGE,"E21"),subQ0,sQuery(id+"F0.wireOp",EDGE,"E23"),sQuery(id+"F0.wireOp",EDGE,"E24"),sQuery(id+"F0.wireOp",EDGE,"E25"),sQuery(id+"F0.wireOp",EDGE,"E26"),sQuery(id+"F0.wireOp",EDGE,"E27"),sQuery(id+"F0.wireOp",EDGE,"uk7PX5xF-f4ir-d9Fz-fdzY-7k4JSw0t9sw8"),sQuery(id+"F0.wireOp",EDGE,"4LPARoRI-8ECf-zc7A-Vkg7-1xuqQKTpim5R"),sQuery(id+"F0.wireOp",EDGE,"JqhvHDZe-7HvT-5HnW-5w5B-O84xCgJDLy5n"),sQuery(id+"F0.wireOp",EDGE,"E28"),sQuery(id+"F0.wireOp",EDGE,"E29"),sQuery(id+"F0.wireOp",EDGE,"E30"),sQuery(id+"F0.wireOp",EDGE,"E31")])],"isStart":true})]});}
            var Q16;
            {var subQ0=sQuery(id+"F0.wireOp",EDGE,"E21");Q16=makeQuery(id+"F3.opChamfer","BLEND_EDGE",EDGE,{"blendedFrom":[makeQuery(id+"F1.opExtrude","CAP_EDGE",EDGE,{"disambiguationData":[OSD([subQ0])],"isStart":false}),makeQuery(id+"F1.opExtrude","SWEPT_FACE",FACE,{"disambiguationData":[OSD([subQ0])]})],"blendedInto":[makeQuery(id+"F1.opExtrude","SWEPT_FACE",FACE,{"disambiguationData":[OSD([subQ0])]})]});}
            var Q17;
            {var subQ0=sQuery(id+"F0.wireOp",EDGE,"E20");Q17=makeQuery(id+"F3.opChamfer","BLEND_EDGE",EDGE,{"blendedFrom":[makeQuery(id+"F1.opExtrude","CAP_EDGE",EDGE,{"disambiguationData":[OSD([subQ0])],"isStart":false}),makeQuery(id+"F1.opExtrude","SWEPT_FACE",FACE,{"disambiguationData":[OSD([subQ0])]})],"blendedInto":[makeQuery(id+"F1.opExtrude","SWEPT_FACE",FACE,{"disambiguationData":[OSD([subQ0])]})]});}
            var Q18;
            {var subQ0=sQuery(id+"F0.wireOp",EDGE,"E20");Q18=makeQuery(id+"F3.opChamfer","BLEND_EDGE",EDGE,{"blendedFrom":[makeQuery(id+"F1.opExtrude","CAP_EDGE",EDGE,{"disambiguationData":[OSD([subQ0])],"isStart":true}),makeQuery(id+"F1.opExtrude","SWEPT_FACE",FACE,{"disambiguationData":[OSD([subQ0])]})],"blendedInto":[makeQuery(id+"F1.opExtrude","SWEPT_FACE",FACE,{"disambiguationData":[OSD([subQ0])]})]});}
            var Q19;
            {var subQ0=sQuery(id+"F0.wireOp",EDGE,"E21");Q19=makeQuery(id+"F3.opChamfer","BLEND_EDGE",EDGE,{"blendedFrom":[makeQuery(id+"F1.opExtrude","CAP_EDGE",EDGE,{"disambiguationData":[OSD([subQ0])],"isStart":true}),makeQuery(id+"F1.opExtrude","SWEPT_FACE",FACE,{"disambiguationData":[OSD([subQ0])]})],"blendedInto":[makeQuery(id+"F1.opExtrude","SWEPT_FACE",FACE,{"disambiguationData":[OSD([subQ0])]})]});}
            var Q20;
            {var subQ0=sQuery(id+"F0.wireOp",EDGE,"E19");Q20=makeQuery(id+"F2.opChamfer","BLEND_EDGE",EDGE,{"blendedFrom":[makeQuery(id+"F1.opExtrude","CAP_EDGE",EDGE,{"disambiguationData":[OSD([subQ0])],"isStart":false}),makeQuery(id+"F1.opExtrude","SWEPT_FACE",FACE,{"disambiguationData":[OSD([subQ0])]})],"blendedInto":[makeQuery(id+"F1.opExtrude","SWEPT_FACE",FACE,{"disambiguationData":[OSD([subQ0])]})]});}
            var Q21;
            {var subQ0=sQuery(id+"F0.wireOp",EDGE,"E19");Q21=makeQuery(id+"F2.opChamfer","BLEND_EDGE",EDGE,{"blendedFrom":[makeQuery(id+"F1.opExtrude","CAP_EDGE",EDGE,{"disambiguationData":[OSD([subQ0])],"isStart":true}),makeQuery(id+"F1.opExtrude","SWEPT_FACE",FACE,{"disambiguationData":[OSD([subQ0])]})],"blendedInto":[makeQuery(id+"F1.opExtrude","SWEPT_FACE",FACE,{"disambiguationData":[OSD([subQ0])]})]});}
            chamfer(context, id + "F4", {"entities" : qUnion([Q0, Q1, Q2, Q3, Q4, Q5, Q6, Q7, Q8, Q9, Q10, Q11, Q12, Q13, Q14, Q15, Q16, Q17, Q18, Q19, Q20, Q21]), "width" : 5.08 * mm, "tangentPropagation" : true});
        }
    });
